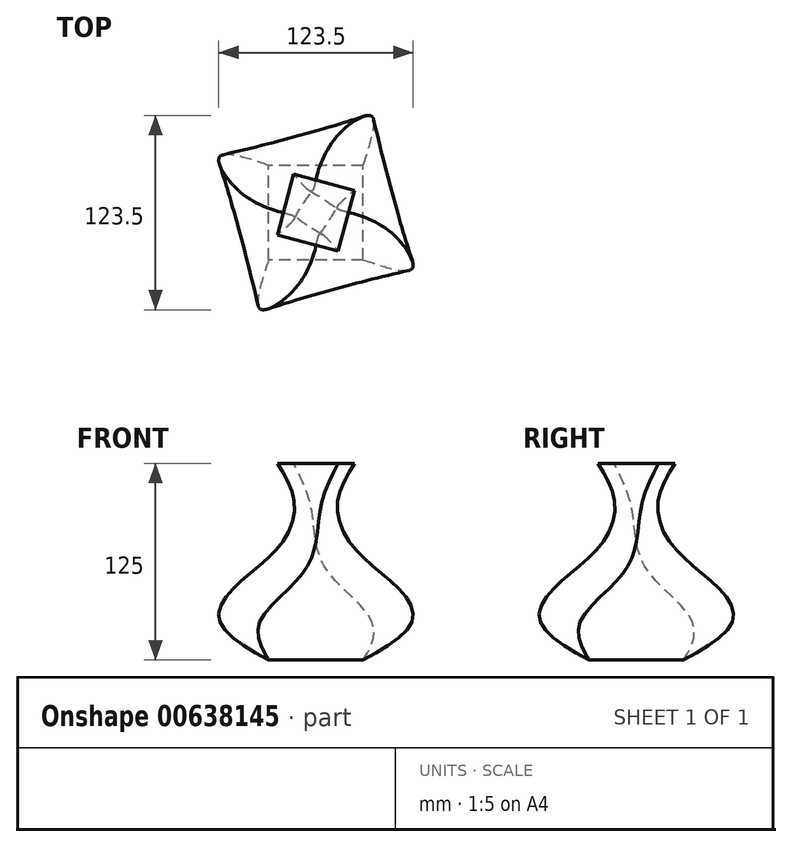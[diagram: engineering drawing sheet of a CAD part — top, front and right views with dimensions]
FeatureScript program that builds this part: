
annotation { "Feature Type Name" : "Feature", "Feature Type Description" : "" }
export const myFeature = defineFeature(function(context is Context, id is Id, definition is map)
    precondition{}
    {
        {
            var Q0;
            Q0=qCreatedBy(makeId("Top.planeOp"),FACE);
            cPlane(context, id + "F0", {"entities" : qUnion([Q0]), "cplaneType" : CPlaneType.OFFSET, "offset" : 25 * mm, "width" : 150 * mm, "height" : 150 * mm});
        }
        {
            var Q0;
            Q0=qCreatedBy(id+"F0.planeOp",FACE);
            cPlane(context, id + "F1", {"entities" : qUnion([Q0]), "cplaneType" : CPlaneType.OFFSET, "offset" : 25 * mm, "width" : 150 * mm, "height" : 150 * mm});
        }
        {
            var Q0;
            Q0=qCreatedBy(id+"F1.planeOp",FACE);
            cPlane(context, id + "F2", {"entities" : qUnion([Q0]), "cplaneType" : CPlaneType.OFFSET, "offset" : 25 * mm, "width" : 150 * mm, "height" : 150 * mm});
        }
        {
            var Q0;
            Q0=qCreatedBy(id+"F2.planeOp",FACE);
            cPlane(context, id + "F3", {"entities" : qUnion([Q0]), "cplaneType" : CPlaneType.OFFSET, "offset" : 25 * mm, "width" : 150 * mm, "height" : 150 * mm});
        }
        {
            var Q0;
            Q0=qCreatedBy(id+"F3.planeOp",FACE);
            cPlane(context, id + "F4", {"entities" : qUnion([Q0]), "cplaneType" : CPlaneType.OFFSET, "offset" : 25 * mm, "width" : 150 * mm, "height" : 150 * mm});
        }
        {
            var Q0;
            Q0=qCreatedBy(makeId("Top.planeOp"),FACE);
            var sketch = newSketch(context, id + "F5", { "sketchPlane" : qUnion([Q0])});
            skLineSegment(sketch, "E0.bottom", {"start": v(30, -30) * mm, "end": v(-30, -30) * mm});
            skLineSegment(sketch, "E0.top", {"start": v(30, 30) * mm, "end": v(-30, 30) * mm});
            skLineSegment(sketch, "E0.left", {"start": v(30, -30) * mm, "end": v(30, 30) * mm});
            skLineSegment(sketch, "E0.right", {"start": v(-30, -30) * mm, "end": v(-30, 30) * mm});
            skPoint(sketch, "E0.middle", {"position": v(0, 0) * mm});
            skSolve(sketch);
        }
        {
            var Q0;
            Q0=qCreatedBy(id+"F0.planeOp",FACE);
            var sketch = newSketch(context, id + "F6", { "sketchPlane" : qUnion([Q0])});
            skLineSegment(sketch, "E1.bottom", {"start": v(61.24, -35.36) * mm, "end": v(-35.36, -61.24) * mm});
            skLineSegment(sketch, "E1.top", {"start": v(35.36, 61.24) * mm, "end": v(-61.24, 35.36) * mm});
            skLineSegment(sketch, "E1.left", {"start": v(61.24, -35.36) * mm, "end": v(35.36, 61.24) * mm});
            skLineSegment(sketch, "E1.right", {"start": v(-35.36, -61.24) * mm, "end": v(-61.24, 35.36) * mm});
            skPoint(sketch, "E1.middle", {"position": v(0, 0) * mm});
            skSolve(sketch);
        }
        {
            var Q0;
            Q0=qCreatedBy(id+"F1.planeOp",FACE);
            var sketch = newSketch(context, id + "F7", { "sketchPlane" : qUnion([Q0])});
            skLineSegment(sketch, "E2.bottom", {"start": v(47.81, -12.81) * mm, "end": v(-12.81, -47.81) * mm});
            skLineSegment(sketch, "E2.top", {"start": v(12.81, 47.81) * mm, "end": v(-47.81, 12.81) * mm});
            skLineSegment(sketch, "E2.left", {"start": v(47.81, -12.81) * mm, "end": v(12.81, 47.81) * mm});
            skLineSegment(sketch, "E2.right", {"start": v(-12.81, -47.81) * mm, "end": v(-47.81, 12.81) * mm});
            skPoint(sketch, "E2.middle", {"position": v(0, 0) * mm});
            skSolve(sketch);
        }
        {
            var Q0;
            Q0=qCreatedBy(id+"F2.planeOp",FACE);
            var sketch = newSketch(context, id + "F8", { "sketchPlane" : qUnion([Q0])});
            skLineSegment(sketch, "E3.bottom", {"start": v(-21.21, 0) * mm, "end": v(0, 21.21) * mm});
            skLineSegment(sketch, "E3.top", {"start": v(0, -21.21) * mm, "end": v(21.21, 0) * mm});
            skLineSegment(sketch, "E3.left", {"start": v(-21.21, 0) * mm, "end": v(0, -21.21) * mm});
            skLineSegment(sketch, "E3.right", {"start": v(0, 21.21) * mm, "end": v(21.21, 0) * mm});
            skPoint(sketch, "E3.middle", {"position": v(0, 0) * mm});
            skSolve(sketch);
        }
        {
            var Q0;
            Q0=qCreatedBy(id+"F3.planeOp",FACE);
            var sketch = newSketch(context, id + "F9", { "sketchPlane" : qUnion([Q0])});
            skLineSegment(sketch, "E4.bottom", {"start": v(-3.66, 13.66) * mm, "end": v(-13.66, -3.66) * mm});
            skLineSegment(sketch, "E4.top", {"start": v(13.66, 3.66) * mm, "end": v(3.66, -13.66) * mm});
            skLineSegment(sketch, "E4.left", {"start": v(-3.66, 13.66) * mm, "end": v(13.66, 3.66) * mm});
            skLineSegment(sketch, "E4.right", {"start": v(-13.66, -3.66) * mm, "end": v(3.66, -13.66) * mm});
            skSolve(sketch);
        }
        {
            var Q0;
            Q0=qCreatedBy(id+"F4.planeOp",FACE);
            var sketch = newSketch(context, id + "F10", { "sketchPlane" : qUnion([Q0])});
            skLineSegment(sketch, "E5.bottom", {"start": v(24.5, 14.14) * mm, "end": v(14.14, -24.5) * mm});
            skLineSegment(sketch, "E5.top", {"start": v(-14.14, 24.5) * mm, "end": v(-24.5, -14.14) * mm});
            skLineSegment(sketch, "E5.left", {"start": v(24.5, 14.14) * mm, "end": v(-14.14, 24.5) * mm});
            skLineSegment(sketch, "E5.right", {"start": v(14.14, -24.5) * mm, "end": v(-24.5, -14.14) * mm});
            skPoint(sketch, "E5.middle", {"position": v(0, 0) * mm});
            skSolve(sketch);
        }
        {
            var Q0;
            Q0=makeQuery(id+"F5.imprint","IMPRINT",FACE,{"disambiguationData":[TD([[makeQuery(id+"F5.imprint","IMPRINT",EDGE,{"derivedFrom":sQuery(id+"F5.wireOp",EDGE,"E0.bottom")}),-1.0]])]});
            var Q1;
            Q1=makeQuery(id+"F6.imprint","IMPRINT",FACE,{"disambiguationData":[TD([[makeQuery(id+"F6.imprint","IMPRINT",EDGE,{"derivedFrom":sQuery(id+"F6.wireOp",EDGE,"E1.bottom")}),-1.0]])]});
            var Q2;
            Q2=makeQuery(id+"F7.imprint","IMPRINT",FACE,{"disambiguationData":[TD([[makeQuery(id+"F7.imprint","IMPRINT",EDGE,{"derivedFrom":sQuery(id+"F7.wireOp",EDGE,"E2.bottom")}),-1.0]])]});
            var Q3;
            Q3=makeQuery(id+"F8.imprint","IMPRINT",FACE,{"disambiguationData":[TD([[makeQuery(id+"F8.imprint","IMPRINT",EDGE,{"derivedFrom":sQuery(id+"F8.wireOp",EDGE,"E3.bottom")}),-1.0]])]});
            var Q4;
            Q4=makeQuery(id+"F9.imprint","IMPRINT",FACE,{"disambiguationData":[TD([[makeQuery(id+"F9.imprint","IMPRINT",EDGE,{"derivedFrom":sQuery(id+"F9.wireOp",EDGE,"E4.bottom")}),1.0]])]});
            var Q5;
            Q5=makeQuery(id+"F10.imprint","IMPRINT",FACE,{"disambiguationData":[TD([[makeQuery(id+"F10.imprint","IMPRINT",EDGE,{"derivedFrom":sQuery(id+"F10.wireOp",EDGE,"E5.bottom")}),-1.0]])]});
            var Q6;
            Q6=sQuery(id+"F5.wireOp",EDGE,"E0.bottom");
            var Q7;
            Q7=sQuery(id+"F6.wireOp",EDGE,"E1.bottom");
            var Q8;
            Q8=sQuery(id+"F7.wireOp",EDGE,"E2.bottom");
            var Q9;
            Q9=sQuery(id+"F8.wireOp",EDGE,"E3.top");
            var Q10;
            Q10=sQuery(id+"F9.wireOp",EDGE,"E4.top");
            var Q11;
            Q11=sQuery(id+"F10.wireOp",EDGE,"E5.bottom");
            loft(context, id + "F11", {"sheetProfilesArray" : [{ "sheetProfileEntities" : qUnion([Q0]) }, { "sheetProfileEntities" : qUnion([Q1]) }, { "sheetProfileEntities" : qUnion([Q2]) }, { "sheetProfileEntities" : qUnion([Q3]) }, { "sheetProfileEntities" : qUnion([Q4]) }, { "sheetProfileEntities" : qUnion([Q5]) }], "wireProfilesArray" : [{ "wireProfileEntities" : qUnion([Q6]) }, { "wireProfileEntities" : qUnion([Q7]) }, { "wireProfileEntities" : qUnion([Q8]) }, { "wireProfileEntities" : qUnion([Q9]) }, { "wireProfileEntities" : qUnion([Q10]) }, { "wireProfileEntities" : qUnion([Q11]) }]});
        }
    });
